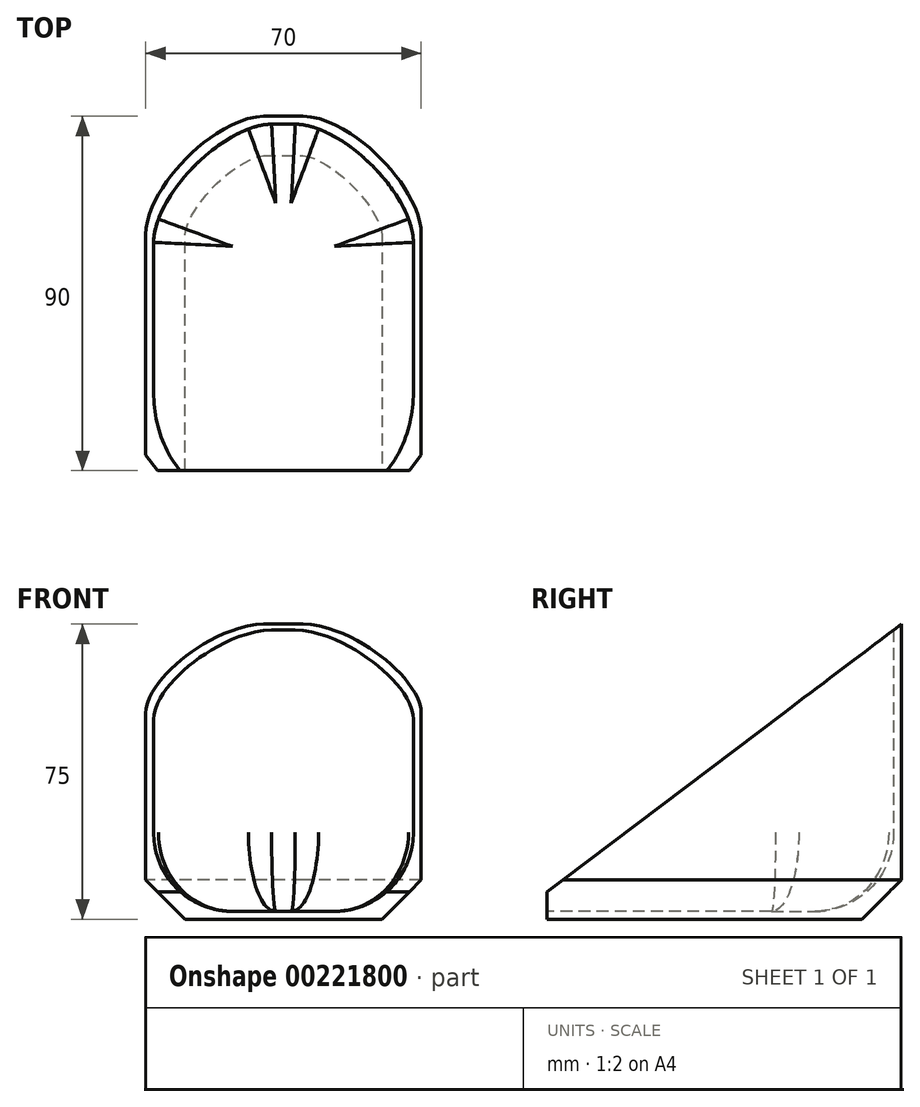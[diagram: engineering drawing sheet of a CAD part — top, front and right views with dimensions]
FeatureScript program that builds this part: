
annotation { "Feature Type Name" : "Feature", "Feature Type Description" : "" }
export const myFeature = defineFeature(function(context is Context, id is Id, definition is map)
    precondition{}
    {
        {
            var Q0;
            Q0=qCreatedBy(makeId("Top.planeOp"),FACE);
            var sketch = newSketch(context, id + "F0", { "sketchPlane" : qUnion([Q0])});
            skLineSegment(sketch, "E0", {"start": v(-35, 0) * mm, "end": v(-35, 90) * mm});
            skLineSegment(sketch, "E1", {"start": v(-35, 90) * mm, "end": v(35, 90) * mm});
            skLineSegment(sketch, "E2", {"start": v(35, 90) * mm, "end": v(35, 0) * mm});
            skLineSegment(sketch, "E3", {"start": v(35, 0) * mm, "end": v(-35, 0) * mm});
            skPoint(sketch, "E4", {"position": v(0, 0) * mm});
            skSolve(sketch);
        }
        {
            var Q0;
            Q0=makeQuery(id+"F0.imprint","IMPRINT",FACE,{"disambiguationData":[TD([[makeQuery(id+"F0.imprint","IMPRINT",EDGE,{"derivedFrom":sQuery(id+"F0.wireOp",EDGE,"E0")}),-1.0]])]});
            extrude(context, id + "F1", {"entities" : qUnion([Q0]), "depth" : 75 * mm});
        }
        {
            var Q0;
            Q0=makeQuery(id+"F1.opExtrude","CAP_FACE",FACE,{"disambiguationData":[OSD([sQuery(id+"F0.wireOp",EDGE,"E0"),sQuery(id+"F0.wireOp",EDGE,"E1"),sQuery(id+"F0.wireOp",EDGE,"E2"),sQuery(id+"F0.wireOp",EDGE,"E3")])],"isStart":false});
            var Q1;
            Q1=makeQuery(id+"F1.opExtrude","SWEPT_FACE",FACE,{"disambiguationData":[OSD([sQuery(id+"F0.wireOp",EDGE,"E3")])]});
            shell(context, id + "F2", {"entities" : qUnion([Q0, Q1]), "thickness" : 2 * mm});
        }
        {
            var Q0;
            Q0=makeQuery(id+"F1.opExtrude","SWEPT_FACE",FACE,{"disambiguationData":[OSD([sQuery(id+"F0.wireOp",EDGE,"E0")])]});
            var sketch = newSketch(context, id + "F3", { "sketchPlane" : qUnion([Q0])});
            skLineSegment(sketch, "E5.0", {"start": v(-90, 75) * mm, "end": v(-90, 0) * mm});
            skLineSegment(sketch, "E5.1", {"start": v(0, 75) * mm, "end": v(0, 0) * mm});
            skLineSegment(sketch, "E5.2", {"start": v(0, 75) * mm, "end": v(-90, 75) * mm});
            skLineSegment(sketch, "E5.3", {"start": v(0, 0) * mm, "end": v(-90, 0) * mm});
            skLineSegment(sketch, "E6", {"start": v(-90, 75) * mm, "end": v(0, 7) * mm});
            skSolve(sketch);
        }
        {
            var Q0;
            {var subQ0=sQuery(id+"F3.wireOp",EDGE,"E5.2");Q0=makeQuery(id+"F3.imprint","IMPRINT",FACE,{"disambiguationData":[TD([[makeQuery(id+"F3.imprint","IMPRINT",EDGE,{"derivedFrom":subQ0}),1.0]])]});}
            var Q1;
            Q1=makeQuery(id+"F1.opExtrude","SWEPT_FACE",FACE,{"disambiguationData":[OSD([sQuery(id+"F0.wireOp",EDGE,"E2")])]});
            extrude(context, id + "F4", {"entities" : qUnion([Q0]), "operationType" : NewBodyOperationType.REMOVE, "endBound" : BoundingType.UP_TO_SURFACE, "oppositeDirection" : true, "endBoundEntityFace" : qUnion([Q1]), "depth" : 25 * mm});
        }
        {
            var Q0;
            Q0=makeQuery(id+"F2.opShell","OFFSET_EDGE",EDGE,{"disambiguationData":[OSD([sQuery(id+"F0.wireOp",EDGE,"E0"),sQuery(id+"F0.wireOp",EDGE,"E1")])]});
            var Q1;
            Q1=makeQuery(id+"F2.opShell","OFFSET_EDGE",EDGE,{"disambiguationData":[OSD([sQuery(id+"F0.wireOp",EDGE,"E1"),sQuery(id+"F0.wireOp",EDGE,"E2")])]});
            fillet(context, id + "F5", {"entities" : qUnion([Q0, Q1]), "radius" : 30 * mm, "tangentPropagation" : true, "rho" : .3, "crossSection" : FilletCrossSection.CONIC, "allowEdgeOverflow" : false});
        }
        {
            var Q0;
            {var subQ0=sQuery(id+"F0.wireOp",EDGE,"E0");Q0=makeQuery(id+"F2.opShell","OFFSET_EDGE",EDGE,{"disambiguationData":[OSD([subQ0]),TDD([makeQuery(id+"F1.opExtrude","CAP_EDGE",EDGE,{"disambiguationData":[OSD([subQ0])],"isStart":true})])]});}
            fillet(context, id + "F6", {"entities" : qUnion([Q0]), "radius" : 20 * mm, "tangentPropagation" : true, "allowEdgeOverflow" : false});
        }
        {
            var Q0;
            Q0=makeQuery(id+"F1.opExtrude","SWEPT_EDGE",EDGE,{"disambiguationData":[OSD([sQuery(id+"F0.wireOp",EDGE,"E1"),sQuery(id+"F0.wireOp",EDGE,"E2")])]});
            var Q1;
            Q1=makeQuery(id+"F1.opExtrude","SWEPT_EDGE",EDGE,{"disambiguationData":[OSD([sQuery(id+"F0.wireOp",EDGE,"E0"),sQuery(id+"F0.wireOp",EDGE,"E1")])]});
            fillet(context, id + "F7", {"entities" : qUnion([Q0, Q1]), "radius" : 30 * mm, "tangentPropagation" : true, "rho" : .3, "crossSection" : FilletCrossSection.CONIC, "allowEdgeOverflow" : false});
        }
        {
            var Q0;
            Q0=makeQuery(id+"F1.opExtrude","CAP_EDGE",EDGE,{"disambiguationData":[OSD([sQuery(id+"F0.wireOp",EDGE,"E0")])],"isStart":true});
            chamfer(context, id + "F8", {"entities" : qUnion([Q0]), "width" : 10 * mm, "tangentPropagation" : true});
        }
    });
